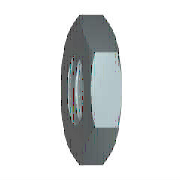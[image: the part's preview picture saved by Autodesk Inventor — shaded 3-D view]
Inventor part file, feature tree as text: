
AUTODESK INVENTOR PART (.ipt)
format: ipt  version: 2020 (Build 240168000, 168)  size: 165,888 bytes
history: native  units: mm (DEFAULTED — no unit token found)
features: sketch x3, chamfer x1, hole x1, other x1, plane x1
ambient origin geometry x7: Origin, YZ Plane, XZ Plane, X Axis, Y Axis, Z Axis, Center Point
bodies: Solid1 (feature_tree), Body (feature_tree)
feature tree (7):
  chamfer  "Chamfer1"  Angle=30.0deg  [1 undecoded]
  hole  "Thread"  [1 undecoded]
  other  "Work Axis1"
  plane  "Work Plane1"
  sketch  "Sketch1"  dims[d0=4.618802mm]
  sketch  "Sketch2"  dims[d1=1.2mm]
  sketch  "Sketch3"  dims[d2=0.0mm d3=30.0deg d4=30.0deg d5=3.1mm d6=3.1mm d7=90.0deg d25=1.567mm d26=6.0mm d27=4.0mm d28=2.0mm d29=14.3117mm d30=8.0mm d31=20.594885mm d8=0.216506mm d9=30.0deg d10=0.216506mm d11=30.0deg d13=0.0mm d14=0.0mm d39=0.0mm d40=0.216506mm d41=0.216506mm d42=0.0mm]
note: 2 required parameter values undecoded (feature->parameter linkage not recoverable at this tier; creation-order binding heuristic only, values carry confidence <= 0.55)
